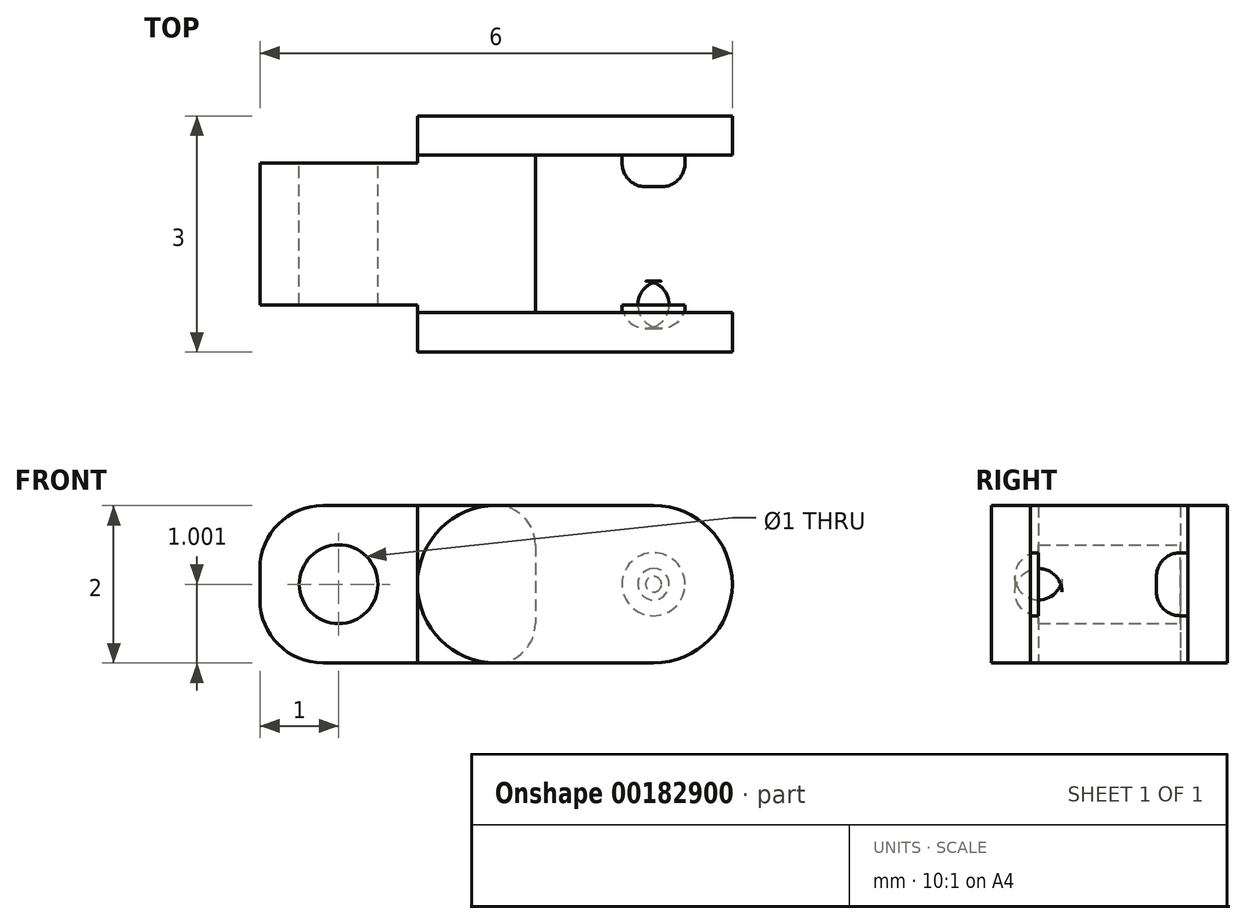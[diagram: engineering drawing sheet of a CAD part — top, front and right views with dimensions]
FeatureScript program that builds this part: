
annotation { "Feature Type Name" : "Feature", "Feature Type Description" : "" }
export const myFeature = defineFeature(function(context is Context, id is Id, definition is map)
    precondition{}
    {
        {
            var Q0;
            Q0=qCreatedBy(makeId("Front.planeOp"),FACE);
            var sketch = newSketch(context, id + "F0", { "sketchPlane" : qUnion([Q0])});
            skLineSegment(sketch, "E0.bottom", {"start": v(-1, -0.25) * mm, "end": v(-5, -0.25) * mm});
            skLineSegment(sketch, "E0.top", {"start": v(-1, -2.25) * mm, "end": v(-5, -2.25) * mm});
            skLineSegment(sketch, "E0.left", {"start": v(-1, -0.25) * mm, "end": v(-1, -2.25) * mm});
            skLineSegment(sketch, "E0.right", {"start": v(-5, -0.25) * mm, "end": v(-5, -2.25) * mm});
            skLineSegment(sketch, "E1", {"start": v(-3, -0.25) * mm, "end": v(-3, -2.25) * mm, "construction": true});
            skArc(sketch, "E2", {"start": v(0, -2.25) * mm, "mid": v(1, -1.25) * mm, "end": v(0, -0.25) * mm});
            skLineSegment(sketch, "E3", {"start": v(-1, -0.25) * mm, "end": v(0, -0.25) * mm});
            skLineSegment(sketch, "E4", {"start": v(-1, -2.25) * mm, "end": v(0, -2.25) * mm});
            skArc(sketch, "E5", {"start": v(-2, -0.25) * mm, "mid": v(-3, -1.25) * mm, "end": v(-2, -2.25) * mm});
            skPoint(sketch, "E6", {"position": v(-4, -1.25) * mm});
            skCircle(sketch, "E7", {"center": v(-4, -1.25) * mm, "radius": 0.5 * mm});
            skCircle(sketch, "E8", {"center": v(0, -1.25) * mm, "radius": 0.4 * mm});
            skCircle(sketch, "E9", {"center": v(0, -1.25) * mm, "radius": 1.41 * mm, "construction": true});
            skLineSegment(sketch, "E10", {"start": v(-1.5, -0.25) * mm, "end": v(-1.5, -1.25) * mm});
            skLineSegment(sketch, "E11", {"start": v(-1.5, -1.25) * mm, "end": v(-1.5, -2.25) * mm});
            skLineSegment(sketch, "E12", {"start": v(0, -0.45) * mm, "end": v(0, -0.25) * mm});
            skSolve(sketch);
        }
        {
            var Q0;
            {var subQ0=sQuery(id+"F0.wireOp",EDGE,"f7VdoiJC-8Tln-2Tbi-K5y5-guD87Exy7ZDr");Q0=makeQuery(id+"F0.imprint","IMPRINT",FACE,{"disambiguationData":[TD([[makeQuery(id+"F0.imprint","IMPRINT",EDGE,{"derivedFrom":subQ0}),-1.0]])]});}
            var Q1;
            {var subQ0=sQuery(id+"F0.wireOp",EDGE,"uH1BQ4Vj-aFWt-8F6M-4EQn-ZlEg98aR2mBw");Q1=makeQuery(id+"F0.imprint","IMPRINT",FACE,{"disambiguationData":[TD([[makeQuery(id+"F0.imprint","IMPRINT",EDGE,{"derivedFrom":subQ0}),1.0]])]});}
            var Q2;
            {var subQ0=sQuery(id+"F0.wireOp",EDGE,"53D6XOHA-X4FV-OfYP-25Ny-iXWlK2nMnlBP");Q2=makeQuery(id+"F0.imprint","IMPRINT",FACE,{"disambiguationData":[TD([[makeQuery(id+"F0.imprint","IMPRINT",EDGE,{"derivedFrom":subQ0}),1.0]])]});}
            var Q3;
            {var subQ3=sQuery(id+"F0.wireOp",EDGE,"mA8XPe0J-LhK4-dBL3-yDRF-5BdcsjTsyDtE");Q3=makeQuery(id+"F0.imprint","IMPRINT",FACE,{"disambiguationData":[TD([[makeQuery(id+"F0.imprint","IMPRINT",EDGE,{"derivedFrom":subQ3}),-1.0]])]});}
            var Q4;
            Q4=makeQuery(id+"F0.imprint","IMPRINT",FACE,{"disambiguationData":[TD([[makeQuery(id+"F0.imprint","IMPRINT",EDGE,{"derivedFrom":sQuery(id+"F0.wireOp",EDGE,"E7")}),1.0]])]});
            var Q5;
            {var subQ6=sQuery(id+"F0.wireOp",EDGE,"E5");Q5=makeQuery(id+"F0.imprint","IMPRINT",FACE,{"disambiguationData":[TD([[makeQuery(id+"F0.imprint","IMPRINT",EDGE,{"derivedFrom":subQ6}),1.0]])]});}
            var Q6;
            {var subQ5=sQuery(id+"F0.wireOp",EDGE,"htJf4tKO-qZep-X4rD-oHbm-76Wo0ydvY8M8.bottom");Q6=makeQuery(id+"F0.imprint","IMPRINT",FACE,{"disambiguationData":[TD([[makeQuery(id+"F0.imprint","IMPRINT",EDGE,{"derivedFrom":subQ5}),-1.0]])]});}
            var Q7;
            {var subQ3=sQuery(id+"F0.wireOp",EDGE,"htJf4tKO-qZep-X4rD-oHbm-76Wo0ydvY8M8.right");Q7=makeQuery(id+"F0.imprint","IMPRINT",FACE,{"disambiguationData":[TD([[makeQuery(id+"F0.imprint","IMPRINT",EDGE,{"derivedFrom":subQ3}),1.0]])]});}
            var Q8;
            {var subQ3=sQuery(id+"F0.wireOp",EDGE,"htJf4tKO-qZep-X4rD-oHbm-76Wo0ydvY8M8.left");Q8=makeQuery(id+"F0.imprint","IMPRINT",FACE,{"disambiguationData":[TD([[makeQuery(id+"F0.imprint","IMPRINT",EDGE,{"derivedFrom":subQ3}),-1.0]])]});}
            var Q9;
            {var subQ1=sQuery(id+"F0.wireOp",EDGE,"E0.right");Q9=makeQuery(id+"F0.imprint","IMPRINT",FACE,{"disambiguationData":[TD([[makeQuery(id+"F0.imprint","IMPRINT",EDGE,{"derivedFrom":subQ1}),1.0]])]});}
            extrude(context, id + "F1", {"entities" : qUnion([Q0, Q1, Q2, Q3, Q4, Q5, Q6, Q7, Q8, Q9]), "depth" : 2 * mm});
        }
        {
            var Q0;
            Q0=makeQuery(id+"F0.imprint","IMPRINT",FACE,{"disambiguationData":[TD([[makeQuery(id+"F0.imprint","IMPRINT",EDGE,{"derivedFrom":sQuery(id+"F0.wireOp",EDGE,"E0.left")}),1.0]])]});
            var Q1;
            {var subQ0=sQuery(id+"F0.wireOp",EDGE,"E0.left");Q1=makeQuery(id+"F0.imprint","IMPRINT",FACE,{"disambiguationData":[TD([[makeQuery(id+"F0.imprint","IMPRINT",EDGE,{"derivedFrom":subQ0}),-1.0]])]});}
            var Q2;
            Q2=makeQuery(id+"F0.imprint","IMPRINT",FACE,{"disambiguationData":[TD([[makeQuery(id+"F0.imprint","IMPRINT",EDGE,{"derivedFrom":sQuery(id+"F0.wireOp",EDGE,"fd2eb06d-ed03-4911-865f-ef9bad8f79ad")}),1.0]])]});
            var Q3;
            {var subQ3=sQuery(id+"F0.wireOp",EDGE,"mA8XPe0J-LhK4-dBL3-yDRF-5BdcsjTsyDtE");Q3=makeQuery(id+"F0.imprint","IMPRINT",FACE,{"disambiguationData":[TD([[makeQuery(id+"F0.imprint","IMPRINT",EDGE,{"derivedFrom":subQ3}),-1.0]])]});}
            var Q4;
            Q4=makeQuery(id+"F0.imprint","IMPRINT",FACE,{"disambiguationData":[TD([[makeQuery(id+"F0.imprint","IMPRINT",EDGE,{"derivedFrom":sQuery(id+"F0.wireOp",EDGE,"E8")}),1.0]])]});
            var Q5;
            {var subQ6=sQuery(id+"F0.wireOp",EDGE,"E5");Q5=makeQuery(id+"F0.imprint","IMPRINT",FACE,{"disambiguationData":[TD([[makeQuery(id+"F0.imprint","IMPRINT",EDGE,{"derivedFrom":subQ6}),1.0]])]});}
            var Q6;
            {var subQ0=sQuery(id+"F0.wireOp",EDGE,"E11");Q6=makeQuery(id+"F0.imprint","IMPRINT",FACE,{"disambiguationData":[TD([[makeQuery(id+"F0.imprint","IMPRINT",EDGE,{"derivedFrom":subQ0}),-1.0]])]});}
            var Q7;
            Q7=makeQuery(id+"F0.imprint","IMPRINT",FACE,{"disambiguationData":[TD([[makeQuery(id+"F0.imprint","IMPRINT",EDGE,{"derivedFrom":sQuery(id+"F0.wireOp",EDGE,"E2")}),1.0]])]});
            var Q8;
            {var subQ0=sQuery(id+"F0.wireOp",EDGE,"E11");Q8=makeQuery(id+"F0.imprint","IMPRINT",FACE,{"disambiguationData":[TD([[makeQuery(id+"F0.imprint","IMPRINT",EDGE,{"derivedFrom":subQ0}),1.0]])]});}
            extrude(context, id + "F2", {"entities" : qUnion([Q0, Q1, Q2, Q3, Q4, Q5, Q6, Q7, Q8]), "operationType" : NewBodyOperationType.ADD, "oppositeDirection" : true, "depth" : 0.5 * mm});
        }
        {
            var Q0;
            Q0=makeQuery(id+"F1.opExtrude","CAP_FACE",FACE,{"disambiguationData":[OSD([sQuery(id+"F0.wireOp",EDGE,"E0.bottom"),sQuery(id+"F0.wireOp",EDGE,"E0.top"),sQuery(id+"F0.wireOp",EDGE,"E0.left"),sQuery(id+"F0.wireOp",EDGE,"E0.right"),sQuery(id+"F0.wireOp",EDGE,"uH1BQ4Vj-aFWt-8F6M-4EQn-ZlEg98aR2mBw"),sQuery(id+"F0.wireOp",EDGE,"kO5BYSIg-LHEv-Mrqp-Hhuf-bGocftPtX9OM"),sQuery(id+"F0.wireOp",EDGE,"f7VdoiJC-8Tln-2Tbi-K5y5-guD87Exy7ZDr"),sQuery(id+"F0.wireOp",EDGE,"Rg8CKrDu-BQip-dAdp-bR6h-5mOOGFjkeTaG")])],"isStart":false});
            var sketch = newSketch(context, id + "F3", { "sketchPlane" : qUnion([Q0])});
            skLineSegment(sketch, "E13", {"start": v(-1, -0.25) * mm, "end": v(-5, -0.25) * mm});
            skArc(sketch, "E14", {"start": v(0, -2.25) * mm, "mid": v(1, -1.25) * mm, "end": v(0, -0.25) * mm});
            skLineSegment(sketch, "E15", {"start": v(-1, -0.25) * mm, "end": v(0, -0.25) * mm});
            skLineSegment(sketch, "E16", {"start": v(-5, -2.25) * mm, "end": v(0, -2.25) * mm});
            skArc(sketch, "E17", {"start": v(-2, -0.25) * mm, "mid": v(-3, -1.25) * mm, "end": v(-2, -2.25) * mm});
            skCircle(sketch, "E18", {"center": v(-4, -1.25) * mm, "radius": 0.5 * mm});
            skCircle(sketch, "E19", {"center": v(0, -1.25) * mm, "radius": 0.4 * mm});
            skSolve(sketch);
        }
        {
            var Q0;
            Q0=makeQuery(id+"F3.imprint","IMPRINT",FACE,{"disambiguationData":[TD([[makeQuery(id+"F3.imprint","IMPRINT",EDGE,{"derivedFrom":sQuery(id+"F3.wireOp",EDGE,"slezlkP0-rkDd-08yD-G4Eu-VJzqF3Z4h6U6")}),1.0]])]});
            var Q1;
            Q1=makeQuery(id+"F3.imprint","IMPRINT",FACE,{"disambiguationData":[TD([[makeQuery(id+"F3.imprint","IMPRINT",EDGE,{"derivedFrom":sQuery(id+"F3.wireOp",EDGE,"slezlkP0-rkDd-08yD-G4Eu-VJzqF3Z4h6U6")}),-1.0]])]});
            var Q2;
            {var subQ0=sQuery(id+"F3.wireOp",EDGE,"E17");Q2=makeQuery(id+"F3.imprint","IMPRINT",FACE,{"disambiguationData":[TD([[makeQuery(id+"F3.imprint","IMPRINT",EDGE,{"derivedFrom":subQ0}),1.0]])]});}
            var Q3;
            Q3=makeQuery(id+"F3.imprint","IMPRINT",FACE,{"disambiguationData":[TD([[makeQuery(id+"F3.imprint","IMPRINT",EDGE,{"derivedFrom":sQuery(id+"F3.wireOp",EDGE,"E14")}),1.0]])]});
            var Q4;
            Q4=makeQuery(id+"F3.imprint","IMPRINT",FACE,{"disambiguationData":[TD([[makeQuery(id+"F3.imprint","IMPRINT",EDGE,{"derivedFrom":sQuery(id+"F3.wireOp",EDGE,"E19")}),1.0]])]});
            var Q5;
            {var subQ1=makeQuery(id+"F1.opExtrude","CAP_EDGE",EDGE,{"disambiguationData":[OSD([sQuery(id+"F0.wireOp",EDGE,"E0.left")])],"isStart":false});Q5=makeQuery(id+"F3.imprint","IMPRINT",FACE,{"disambiguationData":[TD([[makeQuery(id+"F3.imprint","IMPRINT",EDGE,{"derivedFrom":subQ1}),-1.0]])]});}
            extrude(context, id + "F4", {"entities" : qUnion([Q0, Q1, Q2, Q3, Q4, Q5]), "operationType" : NewBodyOperationType.ADD, "depth" : 0.5 * mm});
        }
        {
            var Q0;
            Q0=sQuery(id+"F0.wireOp",VERTEX,"E6");
            var Q1;
            Q1=makeQuery(id+"F1.opExtrude","SWEPT_BODY",BODY,{"disambiguationData":[OSD([sQuery(id+"F0.wireOp",EDGE,"E0.bottom"),sQuery(id+"F0.wireOp",EDGE,"E0.top"),sQuery(id+"F0.wireOp",EDGE,"E0.left"),sQuery(id+"F0.wireOp",EDGE,"E0.right"),sQuery(id+"F0.wireOp",EDGE,"uH1BQ4Vj-aFWt-8F6M-4EQn-ZlEg98aR2mBw"),sQuery(id+"F0.wireOp",EDGE,"kO5BYSIg-LHEv-Mrqp-Hhuf-bGocftPtX9OM"),sQuery(id+"F0.wireOp",EDGE,"f7VdoiJC-8Tln-2Tbi-K5y5-guD87Exy7ZDr"),sQuery(id+"F0.wireOp",EDGE,"Rg8CKrDu-BQip-dAdp-bR6h-5mOOGFjkeTaG"),sQuery(id+"F0.wireOp",EDGE,"mA8XPe0J-LhK4-dBL3-yDRF-5BdcsjTsyDtE")])]});
            hole(context, id + "F5", {"style" : HoleStyle.SIMPLE, "endStyle" : HoleEndStyle.THROUGH, "oppositeDirection" : true, "holeDiameter" : 1 * mm, "locations" : qUnion([Q0]), "scope" : qUnion([Q1]), "isTappedThrough" : true});
        }
        {
            var Q0;
            Q0=makeQuery(id+"F0.imprint","IMPRINT",FACE,{"disambiguationData":[TD([[makeQuery(id+"F0.imprint","IMPRINT",EDGE,{"derivedFrom":sQuery(id+"F0.wireOp",EDGE,"E8")}),1.0]])]});
            extrude(context, id + "F6", {"entities" : qUnion([Q0]), "operationType" : NewBodyOperationType.ADD, "depth" : 0.4 * mm});
        }
        {
            var Q0;
            Q0=makeQuery(id+"F3.imprint","IMPRINT",FACE,{"disambiguationData":[TD([[makeQuery(id+"F3.imprint","IMPRINT",EDGE,{"derivedFrom":sQuery(id+"F3.wireOp",EDGE,"E19")}),1.0]])]});
            extrude(context, id + "F7", {"entities" : qUnion([Q0]), "operationType" : NewBodyOperationType.ADD, "oppositeDirection" : true, "depth" : 0.4 * mm});
        }
        {
            var Q0;
            Q0=makeQuery(id+"F6.opExtrude","CAP_EDGE",EDGE,{"disambiguationData":[OSD([sQuery(id+"F0.wireOp",EDGE,"E8")])],"isStart":false});
            var Q1;
            Q1=makeQuery(id+"F7.opExtrude","CAP_EDGE",EDGE,{"disambiguationData":[OSD([sQuery(id+"F3.wireOp",EDGE,"E19")])],"isStart":false});
            fillet(context, id + "F8", {"entities" : qUnion([Q0, Q1]), "radius" : 0.3 * mm, "tangentPropagation" : true, "allowEdgeOverflow" : false});
        }
        {
            var Q0;
            {var subQ0=sQuery(id+"F0.wireOp",EDGE,"E0.top");Q0=makeQuery(id+"F4.boolean.opBoolean","MERGE",FACE,{"derivedFrom":[makeQuery(id+"F2.boolean.opBoolean","MERGE",FACE,{"derivedFrom":[makeQuery(id+"F1.opExtrude","SWEPT_FACE",FACE,{"disambiguationData":[OSD([subQ0])]}),makeQuery(id+"F2.opExtrude","SWEPT_FACE",FACE,{"disambiguationData":[OSD([subQ0,sQuery(id+"F0.wireOp",EDGE,"E4")])]})]}),makeQuery(id+"F4.opExtrude","SWEPT_FACE",FACE,{"disambiguationData":[OSD([sQuery(id+"F3.wireOp",EDGE,"zInXIRjH-fRHG-3GU0-XYEf-LjIP5AhaiIGm"),sQuery(id+"F3.wireOp",EDGE,"E16")])]})]});}
            var sketch = newSketch(context, id + "F9", { "sketchPlane" : qUnion([Q0])});
            skLineSegment(sketch, "E20.bottom", {"start": v(-3, 2) * mm, "end": v(-5, 2) * mm});
            skLineSegment(sketch, "E20.top", {"start": v(-3, 1.9) * mm, "end": v(-5, 1.9) * mm});
            skLineSegment(sketch, "E20.left", {"start": v(-3, 2) * mm, "end": v(-3, 1.9) * mm});
            skLineSegment(sketch, "E20.right", {"start": v(-5, 2) * mm, "end": v(-5, 1.9) * mm});
            skLineSegment(sketch, "E21.bottom", {"start": v(-3, 0) * mm, "end": v(-5, 0) * mm});
            skLineSegment(sketch, "E21.top", {"start": v(-3, 0.1) * mm, "end": v(-5, 0.1) * mm});
            skLineSegment(sketch, "E21.left", {"start": v(-3, 0) * mm, "end": v(-3, 0.1) * mm});
            skLineSegment(sketch, "E21.right", {"start": v(-5, 0) * mm, "end": v(-5, 0.1) * mm});
            skSolve(sketch);
        }
        {
            var Q0;
            Q0=makeQuery(id+"F9.imprint","IMPRINT",FACE,{"disambiguationData":[TD([[makeQuery(id+"F9.imprint","IMPRINT",EDGE,{"derivedFrom":sQuery(id+"F9.wireOp",EDGE,"E20.bottom")}),1.0]])]});
            var Q1;
            Q1=makeQuery(id+"F9.imprint","IMPRINT",FACE,{"disambiguationData":[TD([[makeQuery(id+"F9.imprint","IMPRINT",EDGE,{"derivedFrom":sQuery(id+"F9.wireOp",EDGE,"E21.bottom")}),-1.0]])]});
            extrude(context, id + "F10", {"entities" : qUnion([Q0, Q1]), "operationType" : NewBodyOperationType.REMOVE, "oppositeDirection" : true, "depth" : 25 * mm});
        }
        {
            var Q0;
            Q0=makeQuery(id+"F10.boolean.opBoolean","COPY",EDGE,{"derivedFrom":makeQuery(id+"F10.opExtrude","SWEPT_EDGE",EDGE,{"disambiguationData":[OSD([sQuery(id+"F0.wireOp",EDGE,"E0.top"),sQuery(id+"F0.wireOp",EDGE,"E0.right"),sQuery(id+"F9.wireOp",EDGE,"E20.top"),sQuery(id+"F9.wireOp",EDGE,"E20.right")])]})});
            var Q1;
            Q1=makeQuery(id+"F10.boolean.opBoolean","COPY",EDGE,{"derivedFrom":makeQuery(id+"F10.opExtrude","SWEPT_EDGE",EDGE,{"disambiguationData":[OSD([sQuery(id+"F0.wireOp",EDGE,"E0.top"),sQuery(id+"F0.wireOp",EDGE,"E0.right"),sQuery(id+"F9.wireOp",EDGE,"E21.top"),sQuery(id+"F9.wireOp",EDGE,"E21.right")])]})});
            var Q2;
            Q2=makeQuery(id+"F1.opExtrude","SWEPT_EDGE",EDGE,{"disambiguationData":[OSD([sQuery(id+"F0.wireOp",EDGE,"E0.bottom"),sQuery(id+"F0.wireOp",EDGE,"E10")])]});
            var Q3;
            Q3=makeQuery(id+"F1.opExtrude","SWEPT_EDGE",EDGE,{"disambiguationData":[OSD([sQuery(id+"F0.wireOp",EDGE,"E0.top"),sQuery(id+"F0.wireOp",EDGE,"E11")])]});
            var Q4;
            Q4=makeQuery(id+"F1.opExtrude","SWEPT_EDGE",EDGE,{"disambiguationData":[OSD([sQuery(id+"F0.wireOp",EDGE,"E10"),sQuery(id+"F0.wireOp",EDGE,"t16F56LC-VUBg-OdEr-BRBj-rz34hXCJSnK6"),sQuery(id+"F0.wireOp",EDGE,"uLMFn6GE-jxci-5nNL-yVyT-isJLdC4N7jqi")])]});
            fillet(context, id + "F11", {"entities" : qUnion([Q0, Q1, Q2, Q3, Q4]), "radius" : .5 * mm, "tangentPropagation" : true, "allowEdgeOverflow" : false});
        }
        {
            var Q0;
            Q0=makeQuery(id+"F1.opExtrude","SWEPT_EDGE",EDGE,{"disambiguationData":[OSD([sQuery(id+"F0.wireOp",EDGE,"E0.bottom"),sQuery(id+"F0.wireOp",EDGE,"E0.right")])]});
            var Q1;
            Q1=makeQuery(id+"F1.opExtrude","SWEPT_EDGE",EDGE,{"disambiguationData":[OSD([sQuery(id+"F0.wireOp",EDGE,"E0.top"),sQuery(id+"F0.wireOp",EDGE,"E0.right")])]});
            fillet(context, id + "F12", {"entities" : qUnion([Q0, Q1]), "radius" : 0.8 * mm, "tangentPropagation" : true, "allowEdgeOverflow" : false});
        }
    });
